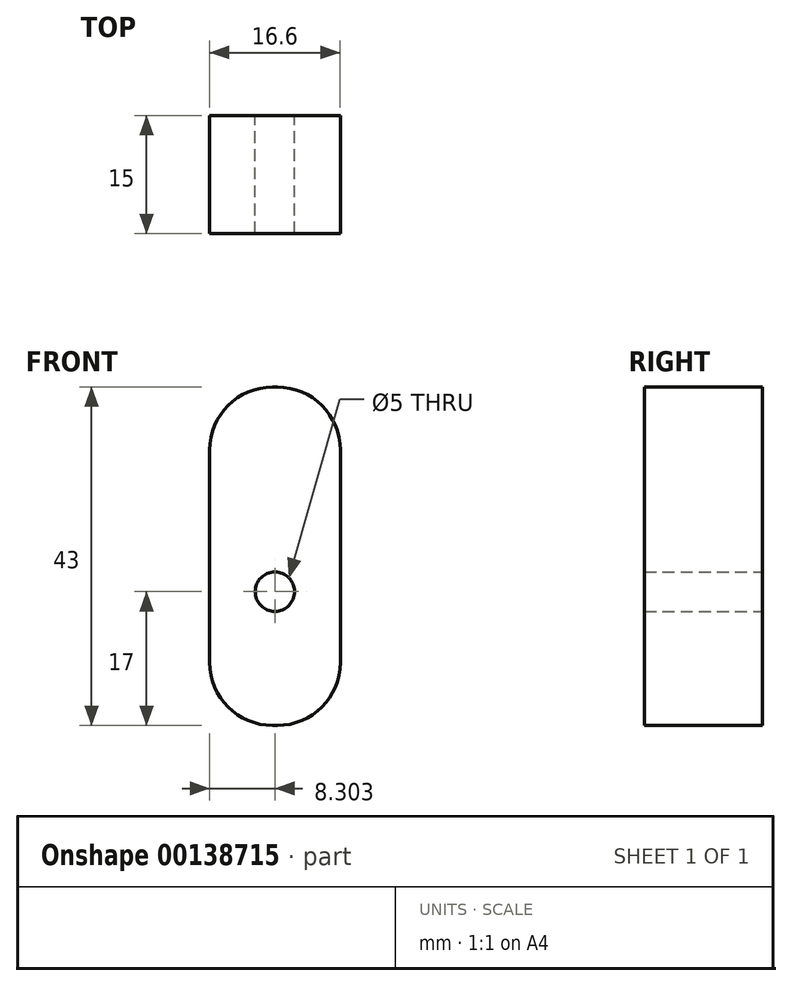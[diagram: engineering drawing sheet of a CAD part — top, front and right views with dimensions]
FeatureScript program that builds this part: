
annotation { "Feature Type Name" : "Feature", "Feature Type Description" : "" }
export const myFeature = defineFeature(function(context is Context, id is Id, definition is map)
    precondition{}
    {
        {
            var Q0;
            Q0=qCreatedBy(makeId("Front.planeOp"),FACE);
            var sketch = newSketch(context, id + "F0", { "sketchPlane" : qUnion([Q0])});
            skLineSegment(sketch, "E0.bottom", {"start": v(-10.43, 23.9) * mm, "end": v(6.17, 23.9) * mm});
            skLineSegment(sketch, "E0.top", {"start": v(-10.43, -19.1) * mm, "end": v(6.17, -19.1) * mm});
            skLineSegment(sketch, "E0.left", {"start": v(-10.43, 23.9) * mm, "end": v(-10.43, -19.1) * mm});
            skLineSegment(sketch, "E0.right", {"start": v(6.17, 23.9) * mm, "end": v(6.17, -19.1) * mm});
            skLineSegment(sketch, "E1", {"start": v(-2.13, 23.9) * mm, "end": v(-2.13, -2.1) * mm, "construction": true});
            skCircle(sketch, "E2", {"center": v(-2.13, -2.1) * mm, "radius": 2.5 * mm});
            skSolve(sketch);
        }
        {
            var Q0;
            Q0 = qSketchRegion(id + "F0", true);
            extrude(context, id + "F1", {"entities" : qUnion([Q0]), "depth" : 15 * mm});
        }
        {
            var Q0;
            Q0=makeQuery(id+"F1.opExtrude","SWEPT_EDGE",EDGE,{"disambiguationData":[OSD([sQuery(id+"F0.wireOp",EDGE,"E0.bottom"),sQuery(id+"F0.wireOp",EDGE,"E0.left")])]});
            var Q1;
            Q1=makeQuery(id+"F1.opExtrude","SWEPT_EDGE",EDGE,{"disambiguationData":[OSD([sQuery(id+"F0.wireOp",EDGE,"E0.top"),sQuery(id+"F0.wireOp",EDGE,"E0.left")])]});
            var Q2;
            Q2=makeQuery(id+"F1.opExtrude","SWEPT_EDGE",EDGE,{"disambiguationData":[OSD([sQuery(id+"F0.wireOp",EDGE,"E0.top"),sQuery(id+"F0.wireOp",EDGE,"E0.right")])]});
            var Q3;
            Q3=makeQuery(id+"F1.opExtrude","SWEPT_EDGE",EDGE,{"disambiguationData":[OSD([sQuery(id+"F0.wireOp",EDGE,"E0.bottom"),sQuery(id+"F0.wireOp",EDGE,"E0.right")])]});
            fillet(context, id + "F2", {"entities" : qUnion([Q0, Q1, Q2, Q3]), "radius" : 8 * mm, "tangentPropagation" : true, "allowEdgeOverflow" : false});
        }
    });
